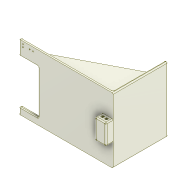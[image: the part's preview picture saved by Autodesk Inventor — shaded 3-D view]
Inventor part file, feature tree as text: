
AUTODESK INVENTOR PART (.ipt)
format: ipt  version: 2021 (Build 250183000, 183)  size: 609,280 bytes
history: native  units: mm
features: other x14, sketch x14, extrude x10, projected_geometry x10, hole x6, fillet x5, mirror x1
ambient origin geometry x8: Origin, YZ Plane, XZ Plane, XY Plane, X Axis, Y Axis, Z Axis, Center Point
bodies: Body1 (feature_tree), Body2 (feature_tree), Body3 (feature_tree)
feature tree (60):
  other  "Твердое тело1"
  extrude  "Выдавливание1"  Depth=350.0mm
  extrude  "Выдавливание2"  Depth=200.0mm
  other  "РабПлоскость5"
  other  "РабПлоскость1"
  extrude  "Выдавливание3"  Depth=10.0mm
  other  "РабПлоскость2"
  other  "Разделение1"
  other  "РабПлоскость4"
  fillet  "Сопряжение2"  Radius=10.0mm
  other  "Разделение2"
  extrude  "Выдавливание4"  Depth=250.0mm TaperAngle=0.0deg
  hole  "Отверстие1"  [1 undecoded]
  fillet  "Сопряжение1"  Radius=27.0mm
  hole  "Отверстие5"  [1 undecoded]
  hole  "Отверстие3"  [1 undecoded]
  extrude  "Выдавливание6"  Depth=3.0mm
  hole  "Отверстие4"  [1 undecoded]
  fillet  "Сопряжение3"  [1 undecoded]
  other  "РабПлоскость6"
  extrude  "Выдавливание8"  [1 undecoded]
  extrude  "Выдавливание9"  Depth=246.0mm TaperAngle=0.0deg
  extrude  "Выдавливание10"  Depth=3.0mm
  fillet  "Сопряжение4"  Radius=4.0mm
  hole  "Отверстие6"  [1 undecoded]
  hole  "Отверстие7"  [1 undecoded]
  extrude  "Выдавливание11"  Depth=78.0mm
  fillet  "Сопряжение5"  Radius=125.0mm
  other  "РабПлоскость8"
  extrude  "Выдавливание13"  TaperAngle=45.0deg  [1 undecoded]
  other  "РабПлоскость9"
  mirror  "Зеркальное отражение1"
  sketch  "Эскиз1"
  sketch  "Эскиз2"
  projected_geometry  "Спроецированная петля1"
  projected_geometry  "Спроецированная петля2"
  sketch  "Эскиз5"
  projected_geometry  "Спроецированная петля4"
  projected_geometry  "Спроецированная петля5"
  sketch  "Эскиз6"
  projected_geometry  "Спроецированная петля6"
  sketch  "Эскиз11"
  projected_geometry  "Спроецированная петля9"
  sketch  "Эскиз12"
  projected_geometry  "Спроецированная петля10"
  sketch  "Эскиз13"
  projected_geometry  "Спроецированная петля11"
  sketch  "Эскиз16"
  sketch  "Эскиз17"
  projected_geometry  "Спроецированная петля12"
  sketch  "Эскиз18"
  projected_geometry  "Спроецированная петля13"
  sketch  "Эскиз19"
  sketch  "Эскиз20"
  sketch  "Эскиз21"
  sketch  "Эскиз23"
  other  "Твердое тело2"
  other  "Твердое тело3"
  other  "Твердое тело4"
  other  "Твердое тело5"
note: 9 required parameter values undecoded (feature->parameter linkage not recoverable at this tier; creation-order binding heuristic only, values carry confidence <= 0.55)
